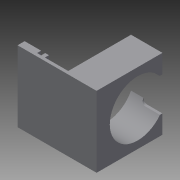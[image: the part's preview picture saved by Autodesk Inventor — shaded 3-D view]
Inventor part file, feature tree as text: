
AUTODESK INVENTOR PART (.ipt)
format: ipt  version: 2015 SP2 (Build 190223200, 223)  size: 173,056 bytes
history: native  units: mm
features: sketch x16, extrude x8, hole x2
ambient origin geometry x8: Origin, YZ Plane, XZ Plane, XY Plane, X Axis, Y Axis, Z Axis, Center Point
bodies: Solid1 (feature_tree)
feature tree (26):
  extrude  "Extrusion1"  Depth=31.0mm
  sketch  "Sketch2"  dims[d2=60.0mm d3=0.0mm d5=55.0mm]
  hole  "Hole1"  [1 undecoded]
  sketch  "Sketch4"  dims[d42=8.0mm d43=8.0mm]
  sketch  "Sketch5"  dims[d44=4.0mm d45=0.0mm d46=4.0mm d47=0.0mm]
  sketch  "Sketch7"  dims[d48=5.0mm d49=6.0mm d50=4.0mm d51=2.0mm d52=90.0deg d53=14.0mm d54=0.0mm d57=47.0mm]
  sketch  "Sketch8"  dims[d63=2.0mm d64=0.0mm d67=5.0mm d68=0.0mm]
  sketch  "Sketch9"  dims[d98=21.0mm d99=0.0mm d120=23.0mm]
  sketch  "Sketch14"  dims[d121=21.0mm d138=4.0mm d139=0.0mm]
  extrude  "Extrusion4"  Depth=4.0mm
  extrude  "Extrusion5"  Depth=8.0mm
  hole  "Hole5"  [1 undecoded]
  sketch  "Sketch18"  dims[d124=1.0mm]
  extrude  "Extrusion9"  Depth=47.0mm
  extrude  "Extrusion11"  Depth=5.0mm TaperAngle=0.0deg
  sketch  "Sketch29"
  extrude  "Extrusion20"  Depth=23.0mm
  sketch  "Sketch37"
  sketch  "Sketch39"
  extrude  "Extrusion25"  Depth=4.0mm TaperAngle=0.0deg
  extrude  "Extrusion26"  Depth=4.0mm TaperAngle=0.0deg
  sketch  "Sketch1"  dims[d0=70.0mm d1=31.0mm]
  sketch  "Sketch3"  dims[d6=55.0mm d7=6.0mm d8=4.0mm d9=2.0mm d10=90.0deg d11=8.0mm d12=20.594885mm d33=4.0mm]
  sketch  "Sketch15"  dims[d140=4.0mm d141=4.0mm d142=0.0mm]
  sketch  "Sketch25"  dims[d125=1.0mm]
  sketch  "Sketch35"
note: 2 required parameter values undecoded (feature->parameter linkage not recoverable at this tier; creation-order binding heuristic only, values carry confidence <= 0.55)
